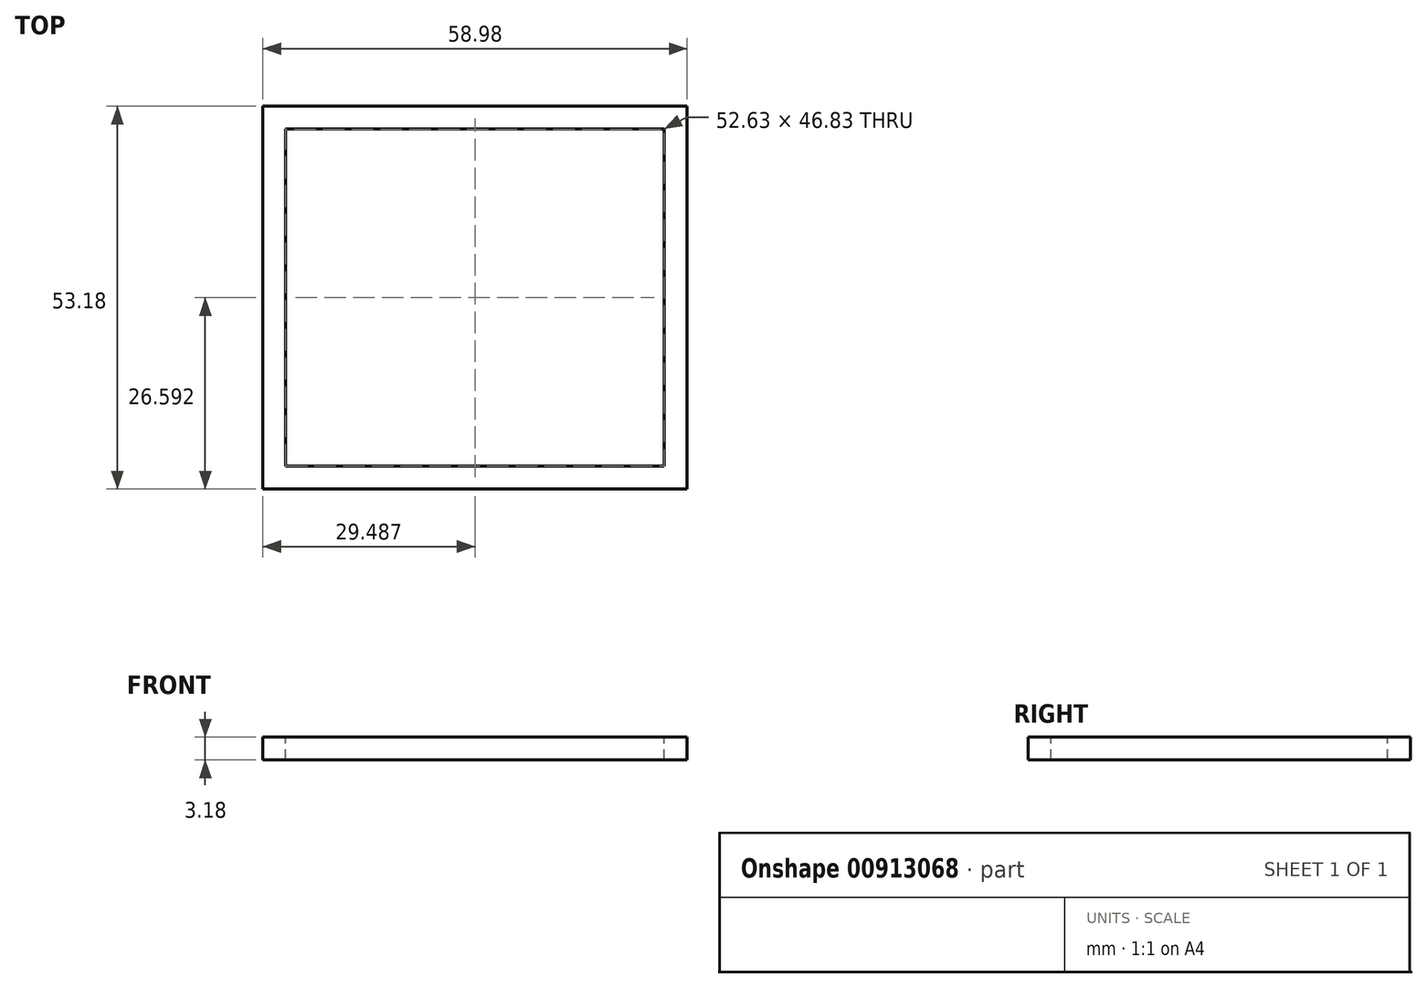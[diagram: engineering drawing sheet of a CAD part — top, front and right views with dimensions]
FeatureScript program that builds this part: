
annotation { "Feature Type Name" : "Feature", "Feature Type Description" : "" }
export const myFeature = defineFeature(function(context is Context, id is Id, definition is map)
    precondition{}
    {
        {
            var Q0;
            Q0=qCreatedBy(makeId("Top.planeOp"),FACE);
            var sketch = newSketch(context, id + "F0", { "sketchPlane" : qUnion([Q0])});
            skLineSegment(sketch, "E0.bottom", {"start": v(-91.5, -61.85) * mm, "end": v(-147.3, -61.85) * mm});
            skLineSegment(sketch, "E0.top", {"start": v(-91.5, -11.85) * mm, "end": v(-147.3, -11.85) * mm});
            skLineSegment(sketch, "E0.left", {"start": v(-91.5, -61.85) * mm, "end": v(-91.5, -11.85) * mm});
            skLineSegment(sketch, "E0.right", {"start": v(-147.3, -61.85) * mm, "end": v(-147.3, -11.85) * mm});
            skSolve(sketch);
        }
        {
            var Q0;
            Q0=sQuery(id+"F0.wireOp",VERTEX,"E0.bottom.end");
            var Q1;
            Q1=sQuery(id+"F0.wireOp",EDGE,"E0.right");
            cPlane(context, id + "F1", {"entities" : qUnion([Q0, Q1]), "cplaneType" : CPlaneType.LINE_POINT, "offset" : 25.4 * mm, "width" : 152.4 * mm, "height" : 152.4 * mm});
        }
        {
            var Q0;
            Q0=qCreatedBy(id+"F1.planeOp",FACE);
            var sketch = newSketch(context, id + "F2", { "sketchPlane" : qUnion([Q0])});
            skLineSegment(sketch, "E1.bottom", {"start": v(148.88, 1.59) * mm, "end": v(145.7, 1.59) * mm});
            skLineSegment(sketch, "E1.top", {"start": v(148.88, -1.59) * mm, "end": v(145.7, -1.59) * mm});
            skLineSegment(sketch, "E1.left", {"start": v(148.88, 1.59) * mm, "end": v(148.88, -1.59) * mm});
            skLineSegment(sketch, "E1.right", {"start": v(145.7, 1.59) * mm, "end": v(145.7, -1.59) * mm});
            skLineSegment(sketch, "E2", {"start": v(148.88, 1.59) * mm, "end": v(145.7, -1.59) * mm, "construction": true});
            skSolve(sketch);
        }
        {
            var Q0;
            Q0=makeQuery(id+"F2.imprint","IMPRINT",FACE,{"disambiguationData":[TD([[makeQuery(id+"F2.imprint","IMPRINT",EDGE,{"derivedFrom":sQuery(id+"F2.wireOp",EDGE,"E1.bottom")}),1.0]])]});
            var Q1;
            Q1=sQuery(id+"F0.wireOp",EDGE,"E0.right");
            var Q2;
            Q2=sQuery(id+"F0.wireOp",EDGE,"E0.top");
            var Q3;
            Q3=sQuery(id+"F0.wireOp",EDGE,"E0.left");
            var Q4;
            Q4=sQuery(id+"F0.wireOp",EDGE,"E0.bottom");
            sweep(context, id + "F3", {"profiles" : qUnion([Q0]), "path" : qUnion([Q1, Q2, Q3, Q4])});
        }
    });
